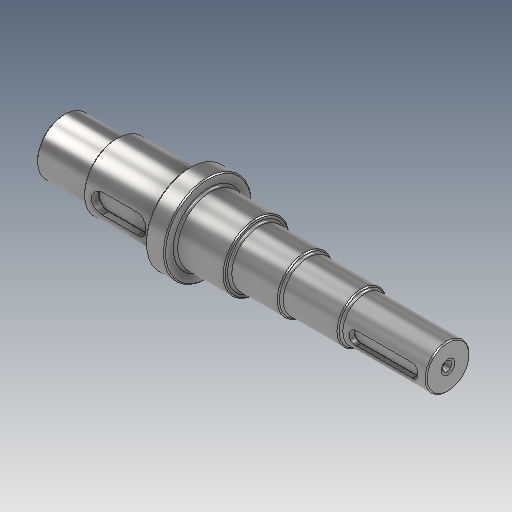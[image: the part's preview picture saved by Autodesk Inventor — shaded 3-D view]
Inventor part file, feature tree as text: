
AUTODESK INVENTOR PART (.ipt)
format: ipt  version: 2025 (Build 290162000, 162)  size: 325,632 bytes
history: native  units: mm
features: other x7, revolve x2, chamfer x1, fillet x1, sketch x1
ambient origin geometry x6: Origin, XZ Plane, XY Plane, X Axis, Y Axis, Z Axis
bodies: 实体1 (feature_tree)
feature tree (12):
  other  "{BB8FE430-83BF-418D-8DF9-9B323D3DB9B9}"
  revolve  "旋转1"  [1 undecoded]
  other  "键槽2"
  other  "键槽3"
  chamfer  "倒角9"  Distance=60.0mm
  fillet  "圆角1"  Radius=80.0mm
  revolve  "旋转2"  [1 undecoded]
  other  "起始平面"
  other  "主草图"
  other  "轴键槽"
  other  "轴键槽2"
  sketch  "草图3"  dims[d0=0.0mm d1=0.0mm d2=0.0mm d3=50.0mm d4=60.0mm d5=80.0mm d6=60.0mm d7=50.0mm d8=45.0mm d9=40.0mm d10=0.0mm d35=1.0mm d36=2.0mm d37=45.0deg d38=2.0mm d39=150.0deg d40=120.0deg d42=6.25mm d43=4.25mm d44=2.0mm d45=5.0mm d46=60.0deg d47=90.0deg]
note: 2 required parameter values undecoded (feature->parameter linkage not recoverable at this tier; creation-order binding heuristic only, values carry confidence <= 0.55)
